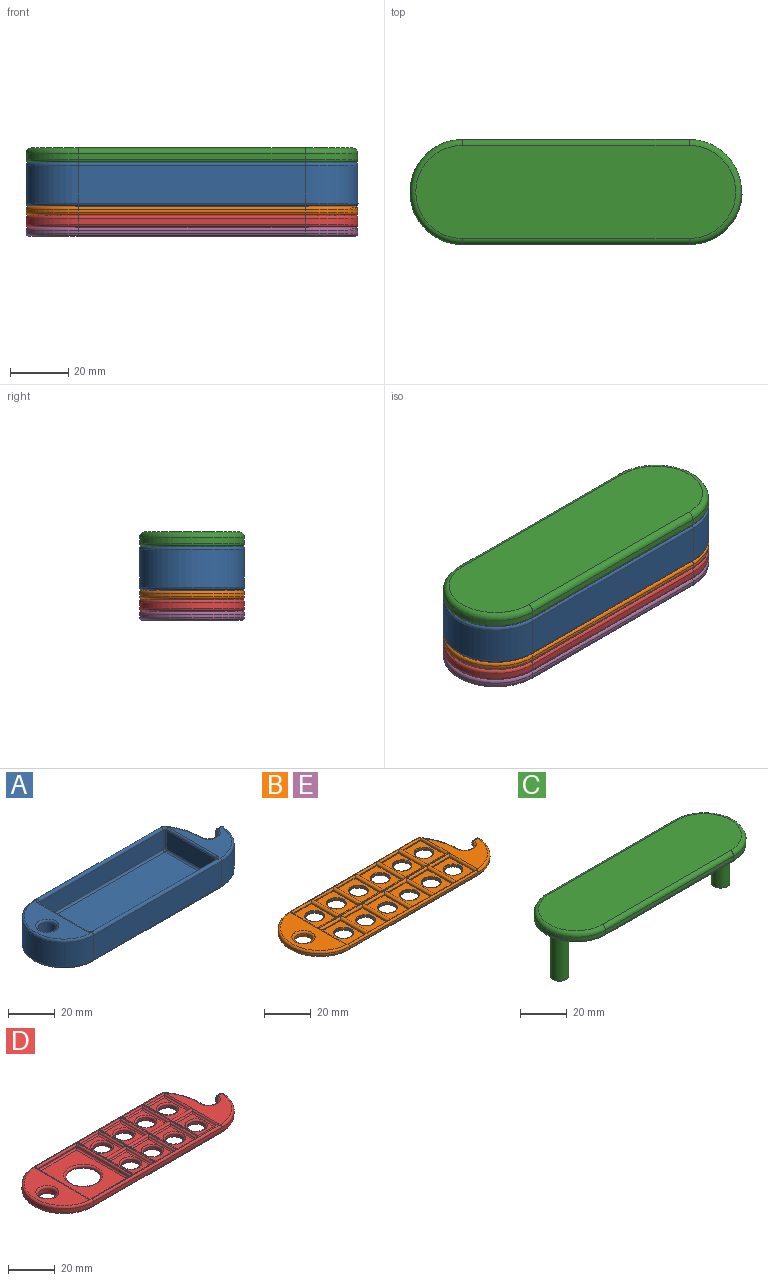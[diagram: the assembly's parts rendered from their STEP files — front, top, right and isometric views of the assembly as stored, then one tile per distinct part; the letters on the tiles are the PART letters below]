
ASSEMBLY  parts=5 mates=4
PART A: 58 faces, bbox 117x39x15 mm
  f0: plane 32.74x18.47mm, normal (0,0,1), area 225.4mm2, adj f28,f33,f34,f36,f37,f38,f50,f54
  f1: plane 1.39x0.57mm, normal (0,0,1), area 0.1mm2, adj f32,f33,f36
  f2: plane 77.49x13mm, normal (0,1,0), area 1007.4mm2, adj f3,f32,f44,f47
  f3: cylinder r=18mm len=36mm, axis (0,0,-1), area 735.1mm2, adj f2,f4,f42,f49
  f4: plane 78x13mm, normal (0,-1,0), area 1014mm2, adj f3,f5,f34,f40
  f5: cylinder r=18mm len=17.97mm, axis (0,0,-1), area 353.8mm2, adj f4,f39,f50,f55
  f6: plane 13x2.07mm, normal (0,1,0), area 26.9mm2, adj f41,f52,f54,f55
  f7: cylinder r=4mm len=13mm, axis (0,0,-1), area 152.9mm2, adj f8,f28,f43,f52
  f8: cylinder r=30mm len=17.59mm, axis (0,0,-1), area 244.3mm2, adj f7,f33,f45,f47
  f9: cylinder r=4mm len=13mm, axis (0,0,-1), area 326.7mm2, adj f51,f57
  f10: plane 111.97x34mm, normal (0,0,-1), area 3268.2mm2, adj f39,f40,f41,f42,f43,f44,f45,f51
  f11: plane 30x10mm, normal (1,0,0), area 300mm2, adj f17,f21,f22,f23
  f12: plane 75.5x10mm, normal (0,-1,0), area 755mm2, adj f20,f21,f31,f32
  f13: plane 30x10mm, normal (-1,0,0), area 300mm2, adj f25,f31,f35,f38
  f14: plane 75.5x10mm, normal (0,1,0), area 755mm2, adj f23,f24,f34,f35
  f15: plane 34x18mm, normal (0,0,1), area 343.1mm2, adj f22,f27,f29,f32,f34,f49,f57
  f16: plane 75.5x30mm, normal (0,0,1), area 2265mm2, adj f17,f20,f24,f25
  f17: cylinder r=1mm len=30mm, axis (0,-1,0), area 47.1mm2, adj f11,f16,f18,f19
  f18: sphere r=1mm, area 1.6mm2, adj f17,f20,f21
  f19: sphere r=1mm, area 1.6mm2, adj f17,f23,f24
  f20: cylinder r=1mm len=75.5mm, axis (-1,0,0), area 118.6mm2, adj f12,f16,f18,f26
  f21: cylinder r=1mm len=10mm, axis (0,0,-1), area 15.7mm2, adj f11,f12,f18,f27
  f22: cylinder r=1mm len=30mm, axis (0,-1,0), area 47.1mm2, adj f11,f15,f27,f29
  f23: cylinder r=1mm len=10mm, axis (0,0,1), area 15.7mm2, adj f11,f14,f19,f29
  f24: cylinder r=1mm len=75.5mm, axis (1,0,0), area 118.6mm2, adj f14,f16,f19,f30
  f25: cylinder r=1mm len=30mm, axis (0,1,0), area 47.1mm2, adj f13,f16,f26,f30
  f26: sphere r=1mm, area 1.6mm2, adj f20,f25,f31
  f27: torus R=2mm, axis (0,0,1), area 3.4mm2, adj f15,f21,f22,f32
  f28: torus R=5mm, axis (0,0,1), area 20.2mm2, adj f0,f7,f33,f53
  f29: torus R=2mm, axis (0,0,1), area 3.4mm2, adj f15,f22,f23,f34
  f30: sphere r=1mm, area 1.6mm2, adj f24,f25,f35
  f31: cylinder r=1mm len=10mm, axis (0,0,1), area 15.7mm2, adj f12,f13,f26,f36
  f32: cylinder r=1mm len=77.49mm, axis (-1,0,0), area 240.3mm2, adj f1,f2,f12,f15,f27,f36,f48,f49
  f33: torus R=29mm, axis (0,0,1), area 29.1mm2, adj f0,f1,f8,f28,f36,f48
  f34: cylinder r=1mm len=78mm, axis (1,0,0), area 241.1mm2, adj f0,f4,f14,f15,f29,f37,f49,f50
  f35: cylinder r=1mm len=10mm, axis (0,0,-1), area 15.7mm2, adj f13,f14,f30,f37
  f36: torus R=2mm, axis (0,0,1), area 3.4mm2, adj f0,f1,f31,f32,f33,f38
  f37: torus R=2mm, axis (0,0,1), area 3.4mm2, adj f0,f34,f35,f38
  f38: cylinder r=1mm len=30mm, axis (0,1,0), area 47.1mm2, adj f0,f13,f36,f37
  f39: torus R=17mm, axis (0,0,1), area 42.5mm2, adj f5,f10,f40,f41,f55
  f40: cylinder r=1mm len=78mm, axis (1,0,0), area 122.5mm2, adj f4,f10,f39,f42
  f41: cylinder r=1mm len=3.45mm, axis (-1,0,0), area 4.4mm2, adj f6,f10,f39,f43,f52,f55
  f42: torus R=17mm, axis (0,0,1), area 87mm2, adj f3,f10,f40,f44
  f43: torus R=5mm, axis (0,0,1), area 20.6mm2, adj f7,f10,f41,f45,f52
  f44: cylinder r=1mm len=77.49mm, axis (-1,0,0), area 121.7mm2, adj f2,f10,f42,f46
  f45: torus R=29mm, axis (0,0,1), area 29.2mm2, adj f8,f10,f43,f46
  f46: sphere r=1mm, area 0.9mm2, adj f44,f45,f47
  f47: cylinder r=1mm len=13mm, axis (0,0,-1), area 12.3mm2, adj f2,f8,f46,f48
  f48: sphere r=1mm, area 0.9mm2, adj f32,f33,f47
  f49: torus R=17mm, axis (0,0,1), area 87mm2, adj f3,f15,f32,f34
  f50: torus R=17mm, axis (0,0,1), area 41.9mm2, adj f0,f5,f34,f56
  f51: torus R=5mm, axis (0,0,1), area 43.1mm2, adj f9,f10
  f52: cylinder r=1mm len=13.66mm, axis (0,0,-1), area 18.3mm2, adj f6,f7,f41,f43,f53
  f53: sphere r=1mm, area 1.4mm2, adj f28,f52,f54
  f54: cylinder r=1mm len=2.07mm, axis (1,0,0), area 3.3mm2, adj f0,f6,f53,f56
  f55: cylinder r=1mm len=13.72mm, axis (0,0,-1), area 21.8mm2, adj f5,f6,f39,f41,f56
  f56: sphere r=1mm, area 1.6mm2, adj f50,f54,f55
  f57: torus R=5mm, axis (0,0,1), area 43.1mm2, adj f9,f15
PART B: 166 faces, bbox 116.9x39x3 mm
  f0: plane 78x1mm, normal (0,1,0), area 78mm2, adj f1,f6,f63,f74
  f1: cylinder r=18mm len=36mm, axis (0,0,-1), area 56.5mm2, adj f0,f2,f75,f90
  f2: plane 78x1mm, normal (0,-1,0), area 78mm2, adj f1,f3,f91,f96
  f3: cylinder r=18mm len=17.97mm, axis (0,0,-1), area 27.2mm2, adj f2,f97,f100,f103
  f4: plane 2.07x1mm, normal (0,1,0), area 2.1mm2, adj f88,f98,f99,f103
  f5: cylinder r=4mm len=7.92mm, axis (0,0,-1), area 11.8mm2, adj f6,f87,f88,f89
  f6: cylinder r=30mm len=18mm, axis (0,0,-1), area 19.3mm2, adj f0,f5,f72,f73
  f7: cylinder r=4mm len=8mm, axis (0,0,-1), area 25.1mm2, adj f104,f105
  f8: plane 111.97x33.95mm, normal (0,0,1), area 588.2mm2, adj f46,f47,f48,f49,f50,f60,f61,f65
  f9: plane 111.97x34mm, normal (0,0,-1), area 2325.7mm2, adj f34,f35,f36,f37,f38,f39,f40,f41
  f10: cylinder r=4mm len=8mm, axis (0,0,-1), area 16.3mm2, adj f44,f160
  f11: plane 14.82x10.82mm, normal (0,0,1), area 103.6mm2, adj f156,f157,f158,f159,f160
  f12: cylinder r=4mm len=8mm, axis (0,0,-1), area 16.3mm2, adj f45,f165
  f13: plane 14.82x10.82mm, normal (0,0,1), area 103.6mm2, adj f161,f162,f163,f164,f165
  f14: cylinder r=4mm len=8mm, axis (0,0,-1), area 16.3mm2, adj f43,f155
  f15: plane 14.82x10.82mm, normal (0,0,1), area 103.6mm2, adj f151,f152,f153,f154,f155
  f16: cylinder r=4mm len=8mm, axis (0,0,-1), area 16.3mm2, adj f40,f140
  f17: plane 14.82x10.82mm, normal (0,0,1), area 103.6mm2, adj f136,f137,f138,f139,f140
  f18: cylinder r=4mm len=8mm, axis (0,0,-1), area 16.3mm2, adj f39,f135
  f19: plane 14.82x10.82mm, normal (0,0,1), area 103.6mm2, adj f131,f132,f133,f134,f135
  f20: cylinder r=4mm len=8mm, axis (0,0,-1), area 16.3mm2, adj f38,f130
  f21: plane 14.82x10.82mm, normal (0,0,1), area 103.6mm2, adj f126,f127,f128,f129,f130
  f22: cylinder r=4mm len=8mm, axis (0,0,-1), area 16.3mm2, adj f34,f110
  f23: plane 14.82x10.82mm, normal (0,0,1), area 103.6mm2, adj f106,f107,f108,f109,f110
  f24: cylinder r=4mm len=8mm, axis (0,0,-1), area 16.3mm2, adj f42,f150
  f25: plane 14.82x10.82mm, normal (0,0,1), area 103.6mm2, adj f146,f147,f148,f149,f150
  f26: cylinder r=4mm len=8mm, axis (0,0,-1), area 16.3mm2, adj f41,f145
  f27: plane 14.82x10.82mm, normal (0,0,1), area 103.6mm2, adj f141,f142,f143,f144,f145
  f28: cylinder r=4mm len=8mm, axis (0,0,-1), area 16.3mm2, adj f37,f125
  f29: plane 14.82x10.82mm, normal (0,0,1), area 103.6mm2, adj f121,f122,f123,f124,f125
  f30: cylinder r=4mm len=8mm, axis (0,0,-1), area 16.3mm2, adj f36,f120
  f31: plane 14.82x10.82mm, normal (0,0,1), area 103.6mm2, adj f116,f117,f118,f119,f120
  f32: cylinder r=4mm len=8mm, axis (0,0,-1), area 16.3mm2, adj f35,f115
  f33: plane 14.82x10.82mm, normal (0,0,1), area 103.6mm2, adj f111,f112,f113,f114,f115
  f34: torus R=5mm, axis (0,0,1), area 43.1mm2, adj f9,f22
  f35: torus R=5mm, axis (0,0,1), area 43.1mm2, adj f9,f32
  f36: torus R=5mm, axis (0,0,1), area 43.1mm2, adj f9,f30
  f37: torus R=5mm, axis (0,0,1), area 43.1mm2, adj f9,f28
  f38: torus R=5mm, axis (0,0,1), area 43.1mm2, adj f9,f20
  f39: torus R=5mm, axis (0,0,1), area 43.1mm2, adj f9,f18
  f40: torus R=5mm, axis (0,0,1), area 43.1mm2, adj f9,f16
  f41: torus R=5mm, axis (0,0,1), area 43.1mm2, adj f9,f26
  f42: torus R=5mm, axis (0,0,1), area 43.1mm2, adj f9,f24
  f43: torus R=5mm, axis (0,0,1), area 43.1mm2, adj f9,f14
  f44: torus R=5mm, axis (0,0,1), area 43.1mm2, adj f9,f10
  f45: torus R=5mm, axis (0,0,1), area 43.1mm2, adj f9,f12
  f46: cylinder r=1mm len=13.3mm, axis (1,0,0), area 17.5mm2, adj f8,f51,f53,f127
  f47: cylinder r=1mm len=13.3mm, axis (1,0,0), area 17.5mm2, adj f8,f53,f55,f132
  f48: cylinder r=1mm len=13.3mm, axis (1,0,0), area 17.5mm2, adj f8,f55,f57,f137
  f49: cylinder r=1mm len=13.3mm, axis (1,0,0), area 17.5mm2, adj f8,f57,f59,f152
  f50: cylinder r=1mm len=13.3mm, axis (1,0,0), area 17.5mm2, adj f8,f51,f61,f107
  f51: cylinder r=1mm len=17.05mm, axis (0,-1,0), area 46.5mm2, adj f46,f50,f52,f62,f63,f109,f126
  f52: cylinder r=1mm len=12.8mm, axis (-1,0,0), area 14.2mm2, adj f51,f53,f63,f128
  f53: cylinder r=1mm len=17.05mm, axis (0,-1,0), area 46.5mm2, adj f46,f47,f52,f54,f63,f129,f131
  f54: cylinder r=1mm len=12.8mm, axis (-1,0,0), area 14.2mm2, adj f53,f55,f63,f133
  f55: cylinder r=1mm len=17.05mm, axis (0,-1,0), area 46.5mm2, adj f47,f48,f54,f56,f63,f134,f136
  f56: cylinder r=1mm len=12.8mm, axis (-1,0,0), area 14.2mm2, adj f55,f57,f63,f138
  f57: cylinder r=1mm len=17.05mm, axis (0,-1,0), area 46.5mm2, adj f48,f49,f56,f58,f63,f139,f151
  f58: cylinder r=1mm len=12.8mm, axis (-1,0,0), area 14.2mm2, adj f57,f59,f63,f153
  f59: cylinder r=1mm len=17.05mm, axis (0,-1,0), area 46.5mm2, adj f49,f58,f60,f63,f64,f154,f158
  f60: cylinder r=1mm len=13.3mm, axis (1,0,0), area 17.5mm2, adj f8,f59,f65,f156
  f61: cylinder r=1mm len=16.73mm, axis (0,1,0), area 22.6mm2, adj f8,f50,f62,f72,f106
  f62: cylinder r=1mm len=12.48mm, axis (-1,0,0), area 14.1mm2, adj f51,f61,f63,f72,f108
  f63: cylinder r=1mm len=78mm, axis (1,0,0), area 103mm2, adj f0,f51,f52,f53,f54,f55,f56,f57
  f64: cylinder r=1mm len=12.79mm, axis (-1,0,0), area 14.2mm2, adj f59,f63,f65,f75,f159
  f65: cylinder r=1mm len=17.04mm, axis (0,-1,0), area 23.3mm2, adj f8,f60,f64,f75,f157
  f66: cylinder r=1mm len=17.04mm, axis (0,-1,0), area 23.3mm2, adj f8,f67,f75,f76,f164
  f67: cylinder r=1mm len=13.3mm, axis (-1,0,0), area 17.5mm2, adj f8,f66,f77,f162
  f68: cylinder r=1mm len=13.3mm, axis (-1,0,0), area 17.5mm2, adj f8,f77,f79,f147
  f69: cylinder r=1mm len=13.3mm, axis (-1,0,0), area 17.5mm2, adj f8,f79,f81,f142
  f70: cylinder r=1mm len=13.3mm, axis (-1,0,0), area 17.5mm2, adj f8,f81,f83,f122
  f71: cylinder r=1mm len=13.3mm, axis (-1,0,0), area 17.5mm2, adj f8,f83,f85,f117
  f72: torus R=29mm, axis (0,0,1), area 28.9mm2, adj f6,f8,f61,f62,f63,f87
  f73: torus R=29mm, axis (0,0,1), area 29.7mm2, adj f6,f9,f74,f89
  f74: cylinder r=1mm len=78mm, axis (-1,0,0), area 122.2mm2, adj f0,f9,f73,f90
  f75: torus R=17mm, axis (0,0,1), area 86.6mm2, adj f1,f8,f63,f64,f65,f66,f76,f91
  f76: cylinder r=1mm len=12.79mm, axis (1,0,0), area 14.2mm2, adj f66,f75,f77,f91,f163
  f77: cylinder r=1mm len=17.05mm, axis (0,1,0), area 46.5mm2, adj f67,f68,f76,f78,f91,f149,f161
  f78: cylinder r=1mm len=12.8mm, axis (1,0,0), area 14.2mm2, adj f77,f79,f91,f148
  f79: cylinder r=1mm len=17.05mm, axis (0,1,0), area 46.5mm2, adj f68,f69,f78,f80,f91,f144,f146
  f80: cylinder r=1mm len=12.8mm, axis (1,0,0), area 14.2mm2, adj f79,f81,f91,f143
  f81: cylinder r=1mm len=17.05mm, axis (0,1,0), area 46.5mm2, adj f69,f70,f80,f82,f91,f124,f141
  f82: cylinder r=1mm len=12.8mm, axis (1,0,0), area 14.2mm2, adj f81,f83,f91,f123
  f83: cylinder r=1mm len=17.05mm, axis (0,1,0), area 46.5mm2, adj f70,f71,f82,f84,f91,f119,f121
  f84: cylinder r=1mm len=12.8mm, axis (1,0,0), area 14.2mm2, adj f83,f85,f91,f118
  f85: cylinder r=1mm len=17.05mm, axis (0,1,0), area 46.5mm2, adj f71,f84,f86,f91,f92,f114,f116
  f86: cylinder r=1mm len=13.3mm, axis (-1,0,0), area 17.5mm2, adj f8,f85,f93,f112
  f87: torus R=5mm, axis (0,0,1), area 20.2mm2, adj f5,f8,f72,f94
  f88: cylinder r=1mm len=1mm, axis (0,0,-1), area 1.4mm2, adj f4,f5,f94,f95
  f89: torus R=5mm, axis (0,0,1), area 20.2mm2, adj f5,f9,f73,f95
  f90: torus R=17mm, axis (0,0,1), area 87mm2, adj f1,f9,f74,f96
  f91: cylinder r=1mm len=78mm, axis (-1,0,0), area 103.1mm2, adj f2,f75,f76,f77,f78,f79,f80,f81
  f92: cylinder r=1mm len=12.8mm, axis (1,0,0), area 14.2mm2, adj f85,f91,f93,f97,f113
  f93: cylinder r=1mm len=17.05mm, axis (0,1,0), area 23.3mm2, adj f8,f86,f92,f97,f111
  f94: sphere r=1mm, area 1.4mm2, adj f87,f88,f98
  f95: sphere r=1mm, area 1.4mm2, adj f88,f89,f99
  f96: cylinder r=1mm len=78mm, axis (1,0,0), area 122.5mm2, adj f2,f9,f90,f100
  f97: torus R=17mm, axis (0,0,1), area 41.7mm2, adj f3,f8,f91,f92,f93,f101
  f98: cylinder r=1mm len=2.07mm, axis (1,0,0), area 3.3mm2, adj f4,f8,f94,f101
  f99: cylinder r=1mm len=2.07mm, axis (-1,0,0), area 3.3mm2, adj f4,f9,f95,f102
  f100: torus R=17mm, axis (0,0,1), area 41.9mm2, adj f3,f9,f96,f102
  f101: sphere r=1mm, area 1.6mm2, adj f97,f98,f103
  f102: sphere r=1mm, area 1.6mm2, adj f99,f100,f103
  f103: cylinder r=1mm len=1.06mm, axis (0,0,-1), area 1.6mm2, adj f3,f4,f101,f102
  f104: torus R=5mm, axis (0,0,1), area 43.1mm2, adj f7,f9
  f105: torus R=5mm, axis (0,0,1), area 43.1mm2, adj f7,f8
  f106: cylinder r=0.25mm len=15.31mm, axis (0,1,0), area 5.5mm2, adj f23,f61,f107,f108
  f107: cylinder r=0.25mm len=11.31mm, axis (1,0,0), area 4mm2, adj f23,f50,f106,f109
  f108: cylinder r=0.25mm len=11.31mm, axis (-1,0,0), area 4mm2, adj f23,f62,f106,f109
  f109: cylinder r=0.25mm len=15.31mm, axis (0,-1,0), area 5.5mm2, adj f23,f51,f107,f108
  f110: torus R=4.25mm, axis (0,0,1), area 10.1mm2, adj f22,f23
  f111: cylinder r=0.25mm len=15.31mm, axis (0,1,0), area 5.5mm2, adj f33,f93,f112,f113
  f112: cylinder r=0.25mm len=11.31mm, axis (-1,0,0), area 4mm2, adj f33,f86,f111,f114
  f113: cylinder r=0.25mm len=11.31mm, axis (1,0,0), area 4mm2, adj f33,f92,f111,f114
  f114: cylinder r=0.25mm len=15.31mm, axis (0,1,0), area 5.5mm2, adj f33,f85,f112,f113
  f115: torus R=4.25mm, axis (0,0,1), area 10.1mm2, adj f32,f33
  f116: cylinder r=0.25mm len=15.31mm, axis (0,1,0), area 5.5mm2, adj f31,f85,f117,f118
  f117: cylinder r=0.25mm len=11.31mm, axis (-1,0,0), area 4mm2, adj f31,f71,f116,f119
  f118: cylinder r=0.25mm len=11.31mm, axis (1,0,0), area 4mm2, adj f31,f84,f116,f119
  f119: cylinder r=0.25mm len=15.31mm, axis (0,1,0), area 5.5mm2, adj f31,f83,f117,f118
  f120: torus R=4.25mm, axis (0,0,1), area 10.1mm2, adj f30,f31
  f121: cylinder r=0.25mm len=15.31mm, axis (0,1,0), area 5.5mm2, adj f29,f83,f122,f123
  f122: cylinder r=0.25mm len=11.31mm, axis (-1,0,0), area 4mm2, adj f29,f70,f121,f124
  f123: cylinder r=0.25mm len=11.31mm, axis (1,0,0), area 4mm2, adj f29,f82,f121,f124
  f124: cylinder r=0.25mm len=15.31mm, axis (0,1,0), area 5.5mm2, adj f29,f81,f122,f123
  f125: torus R=4.25mm, axis (0,0,1), area 10.1mm2, adj f28,f29
  f126: cylinder r=0.25mm len=15.31mm, axis (0,-1,0), area 5.5mm2, adj f21,f51,f127,f128
  f127: cylinder r=0.25mm len=11.31mm, axis (1,0,0), area 4mm2, adj f21,f46,f126,f129
  f128: cylinder r=0.25mm len=11.31mm, axis (-1,0,0), area 4mm2, adj f21,f52,f126,f129
  f129: cylinder r=0.25mm len=15.31mm, axis (0,-1,0), area 5.5mm2, adj f21,f53,f127,f128
  f130: torus R=4.25mm, axis (0,0,1), area 10.1mm2, adj f20,f21
  f131: cylinder r=0.25mm len=15.31mm, axis (0,-1,0), area 5.5mm2, adj f19,f53,f132,f133
  f132: cylinder r=0.25mm len=11.31mm, axis (1,0,0), area 4mm2, adj f19,f47,f131,f134
  f133: cylinder r=0.25mm len=11.31mm, axis (-1,0,0), area 4mm2, adj f19,f54,f131,f134
  f134: cylinder r=0.25mm len=15.31mm, axis (0,-1,0), area 5.5mm2, adj f19,f55,f132,f133
  f135: torus R=4.25mm, axis (0,0,1), area 10.1mm2, adj f18,f19
  f136: cylinder r=0.25mm len=15.31mm, axis (0,-1,0), area 5.5mm2, adj f17,f55,f137,f138
  f137: cylinder r=0.25mm len=11.31mm, axis (1,0,0), area 4mm2, adj f17,f48,f136,f139
  f138: cylinder r=0.25mm len=11.31mm, axis (-1,0,0), area 4mm2, adj f17,f56,f136,f139
  f139: cylinder r=0.25mm len=15.31mm, axis (0,-1,0), area 5.5mm2, adj f17,f57,f137,f138
  f140: torus R=4.25mm, axis (0,0,1), area 10.1mm2, adj f16,f17
  f141: cylinder r=0.25mm len=15.31mm, axis (0,1,0), area 5.5mm2, adj f27,f81,f142,f143
  f142: cylinder r=0.25mm len=11.31mm, axis (-1,0,0), area 4mm2, adj f27,f69,f141,f144
  f143: cylinder r=0.25mm len=11.31mm, axis (1,0,0), area 4mm2, adj f27,f80,f141,f144
  f144: cylinder r=0.25mm len=15.31mm, axis (0,1,0), area 5.5mm2, adj f27,f79,f142,f143
  f145: torus R=4.25mm, axis (0,0,1), area 10.1mm2, adj f26,f27
  f146: cylinder r=0.25mm len=15.31mm, axis (0,1,0), area 5.5mm2, adj f25,f79,f147,f148
  f147: cylinder r=0.25mm len=11.31mm, axis (-1,0,0), area 4mm2, adj f25,f68,f146,f149
  f148: cylinder r=0.25mm len=11.31mm, axis (1,0,0), area 4mm2, adj f25,f78,f146,f149
  f149: cylinder r=0.25mm len=15.31mm, axis (0,1,0), area 5.5mm2, adj f25,f77,f147,f148
  f150: torus R=4.25mm, axis (0,0,1), area 10.1mm2, adj f24,f25
  f151: cylinder r=0.25mm len=15.31mm, axis (0,-1,0), area 5.5mm2, adj f15,f57,f152,f153
  f152: cylinder r=0.25mm len=11.31mm, axis (1,0,0), area 4mm2, adj f15,f49,f151,f154
  f153: cylinder r=0.25mm len=11.31mm, axis (-1,0,0), area 4mm2, adj f15,f58,f151,f154
  f154: cylinder r=0.25mm len=15.31mm, axis (0,-1,0), area 5.5mm2, adj f15,f59,f152,f153
  f155: torus R=4.25mm, axis (0,0,1), area 10.1mm2, adj f14,f15
  f156: cylinder r=0.25mm len=11.31mm, axis (1,0,0), area 4mm2, adj f11,f60,f157,f158
  f157: cylinder r=0.25mm len=15.31mm, axis (0,-1,0), area 5.5mm2, adj f11,f65,f156,f159
  f158: cylinder r=0.25mm len=15.31mm, axis (0,-1,0), area 5.5mm2, adj f11,f59,f156,f159
  f159: cylinder r=0.25mm len=11.31mm, axis (-1,0,0), area 4mm2, adj f11,f64,f157,f158
  f160: torus R=4.25mm, axis (0,0,1), area 10.1mm2, adj f10,f11
  f161: cylinder r=0.25mm len=15.31mm, axis (0,1,0), area 5.5mm2, adj f13,f77,f162,f163
  f162: cylinder r=0.25mm len=11.31mm, axis (-1,0,0), area 4mm2, adj f13,f67,f161,f164
  f163: cylinder r=0.25mm len=11.31mm, axis (1,0,0), area 4mm2, adj f13,f76,f161,f164
  f164: cylinder r=0.25mm len=15.31mm, axis (0,-1,0), area 5.5mm2, adj f13,f66,f162,f163
  f165: torus R=4.25mm, axis (0,0,1), area 10.1mm2, adj f12,f13
PART C: 26 faces, bbox 116.8x39x30 mm
  f0: cylinder r=18mm len=36mm, axis (0,0,-1), area 113.1mm2, adj f1,f3,f18,f24
  f1: plane 77.81x2mm, normal (0,1,0), area 155.6mm2, adj f0,f2,f19,f22
  f2: cylinder r=18mm len=36mm, axis (0,0,-1), area 113.1mm2, adj f1,f3,f21,f23
  f3: plane 77.81x2mm, normal (0,-1,0), area 155.6mm2, adj f0,f2,f20,f25
  f4: plane 109.81x32mm, normal (0,0,1), area 3294.2mm2, adj f22,f23,f24,f25
  f5: plane 111.81x34mm, normal (0,0,-1), area 3396.4mm2, adj f14,f16,f18,f19,f20,f21
  f6: cylinder r=2mm len=24mm, axis (0,0,1), area 301.6mm2, adj f8,f17
  f7: cylinder r=4mm len=24mm, axis (0,0,1), area 603.2mm2, adj f8,f16
  f8: plane 8x8mm, normal (0,0,-1), area 37.7mm2, adj f6,f7
  f9: plane 2x2mm, normal (0,0,-1), area 3.1mm2, adj f17
  f10: cylinder r=2mm len=24mm, axis (0,0,1), area 301.6mm2, adj f12,f15
  f11: cylinder r=4mm len=24mm, axis (0,0,1), area 603.2mm2, adj f12,f14
  f12: plane 8x8mm, normal (0,0,-1), area 37.7mm2, adj f10,f11
  f13: plane 2x2mm, normal (0,0,-1), area 3.1mm2, adj f15
  f14: torus R=5mm, axis (0,0,1), area 43.1mm2, adj f5,f11
  f15: torus R=1mm, axis (0,0,1), area 16.2mm2, adj f10,f13
  f16: torus R=5mm, axis (0,0,1), area 43.1mm2, adj f5,f7
  f17: torus R=1mm, axis (0,0,1), area 16.2mm2, adj f6,f9
  f18: torus R=17mm, axis (0,0,1), area 87mm2, adj f0,f5,f19,f20
  f19: cylinder r=1mm len=77.81mm, axis (-1,0,0), area 122.2mm2, adj f1,f5,f18,f21
  f20: cylinder r=1mm len=77.81mm, axis (1,0,0), area 122.2mm2, adj f3,f5,f18,f21
  f21: torus R=17mm, axis (0,0,1), area 87mm2, adj f2,f5,f19,f20
  f22: cylinder r=2mm len=77.81mm, axis (1,0,0), area 244.4mm2, adj f1,f4,f23,f24
  f23: torus R=16mm, axis (0,0,1), area 170.5mm2, adj f2,f4,f22,f25
  f24: torus R=16mm, axis (0,0,1), area 170.5mm2, adj f0,f4,f22,f25
  f25: cylinder r=2mm len=77.81mm, axis (-1,0,0), area 244.4mm2, adj f3,f4,f23,f24
PART D: 144 faces, bbox 116.9x39x4.3 mm
  f0: plane 34x0.3mm, normal (0,0,1), area 10.2mm2, adj f51,f55,f85,f88,f93,f97
  f1: plane 34x0.3mm, normal (0,0,1), area 10.2mm2, adj f51,f55,f78,f81,f92,f94
  f2: plane 34x30.12mm, normal (0,0,1), area 262mm2, adj f13,f48,f49,f51,f52,f54,f55,f72
  f3: plane 32.3x0.4mm, normal (1,0,0), area 12.9mm2, adj f4,f14,f69,f98
  f4: plane 24.3x0.4mm, normal (0,-1,0), area 9.7mm2, adj f3,f5,f68,f99,f100
  f5: plane 32.3x0.4mm, normal (-1,0,0), area 12.9mm2, adj f4,f14,f70,f101
  f6: cylinder r=4mm len=7.92mm, axis (0,0,-1), area 24mm2, adj f7,f42,f47,f52
  f7: cylinder r=25mm len=17.77mm, axis (0,0,-1), area 38.4mm2, adj f6,f8,f40,f54
  f8: plane 78x2mm, normal (0,1,0), area 156mm2, adj f7,f9,f38,f55
  f9: cylinder r=18mm len=36mm, axis (0,0,-1), area 113.1mm2, adj f8,f10,f36,f53
  f10: plane 78x2mm, normal (0,-1,0), area 156mm2, adj f9,f11,f37,f51
  f11: cylinder r=18mm len=17.97mm, axis (0,0,-1), area 54.4mm2, adj f10,f39,f44,f49
  f12: cylinder r=4mm len=8mm, axis (0,0,-1), area 50.3mm2, adj f65,f66
  f13: plane 13x0.4mm, normal (0,1,0), area 4.8mm2, adj f2,f72,f73,f120
  f14: plane 24.3x0.45mm, normal (0,1,0), area 10.9mm2, adj f3,f5,f71,f98,f101,f143
  f15: plane 2.07x2mm, normal (0,1,0), area 4.1mm2, adj f43,f44,f47,f48
  f16: plane 42.25x34mm, normal (0,0,1), area 351.2mm2, adj f51,f53,f55,f66,f86,f90,f98,f101
  f17: plane 111.97x34mm, normal (0,0,-1), area 2416.9mm2, adj f36,f37,f38,f39,f40,f42,f43,f56
  f18: cylinder r=7.5mm len=15mm, axis (0,0,-1), area 2.4mm2, adj f64,f67
  f19: plane 30.6x22.6mm, normal (0,0,1), area 472.5mm2, adj f67,f68,f69,f70,f71
  f20: cylinder r=4mm len=8mm, axis (0,0,-1), area 25.1mm2, adj f61,f132
  f21: plane 13.83x9.83mm, normal (0,0,1), area 63.5mm2, adj f128,f129,f130,f131,f132
  f22: cylinder r=4mm len=8mm, axis (0,0,-1), area 25.1mm2, adj f58,f117
  f23: plane 13.83x9.83mm, normal (0,0,1), area 63.5mm2, adj f113,f114,f115,f116,f117
  f24: cylinder r=4mm len=8mm, axis (0,0,-1), area 25.1mm2, adj f60,f127
  f25: plane 13.83x9.81mm, normal (0,0,1), area 63.3mm2, adj f123,f124,f125,f126,f127
  f26: cylinder r=4mm len=8mm, axis (0,0,-1), area 25.1mm2, adj f59,f122
  f27: plane 13.76x9.83mm, normal (0,0,1), area 62.8mm2, adj f118,f119,f120,f121,f122
  f28: cylinder r=4mm len=8mm, axis (0,0,-1), area 25.1mm2, adj f56,f107
  f29: plane 13.83x9.83mm, normal (0,0,1), area 63.5mm2, adj f103,f104,f105,f106,f107
  f30: cylinder r=4mm len=8mm, axis (0,0,-1), area 25.1mm2, adj f62,f133
  f31: plane 13.83x9.83mm, normal (0,0,1), area 63.5mm2, adj f133,f134,f135,f136,f137
  f32: cylinder r=4mm len=8mm, axis (0,0,-1), area 25.1mm2, adj f57,f112
  f33: plane 13.83x9.83mm, normal (0,0,1), area 63.5mm2, adj f108,f109,f110,f111,f112
  f34: cylinder r=4mm len=8mm, axis (0,0,-1), area 25.1mm2, adj f63,f142
  f35: plane 13.83x9.83mm, normal (0,0,1), area 63.5mm2, adj f138,f139,f140,f141,f142
  f36: torus R=17mm, axis (0,0,1), area 87mm2, adj f9,f17,f37,f38
  f37: cylinder r=1mm len=78mm, axis (1,0,0), area 122.5mm2, adj f10,f17,f36,f39
  f38: cylinder r=1mm len=78mm, axis (-1,0,0), area 122.2mm2, adj f8,f17,f36,f40
  f39: torus R=17mm, axis (0,0,1), area 41.9mm2, adj f11,f17,f37,f41
  f40: torus R=24mm, axis (0,0,1), area 29.4mm2, adj f7,f17,f38,f42
  f41: sphere r=1mm, area 2.2mm2, adj f39,f43,f44
  f42: torus R=5mm, axis (0,0,1), area 20.6mm2, adj f6,f17,f40,f45
  f43: cylinder r=1mm len=2.07mm, axis (-1,0,0), area 3.3mm2, adj f15,f17,f41,f45
  f44: cylinder r=1mm len=2mm, axis (0,0,-1), area 3.3mm2, adj f11,f15,f41,f46
  f45: sphere r=1mm, area 1.4mm2, adj f42,f43,f47
  f46: sphere r=1mm, area 1.6mm2, adj f44,f48,f49
  f47: cylinder r=1mm len=2mm, axis (0,0,-1), area 2.7mm2, adj f6,f15,f45,f50
  f48: cylinder r=1mm len=2.07mm, axis (1,0,0), area 3.3mm2, adj f2,f15,f46,f50
  f49: torus R=17mm, axis (0,0,1), area 41.9mm2, adj f2,f11,f46,f51
  f50: sphere r=1mm, area 2.6mm2, adj f47,f48,f52
  f51: cylinder r=1mm len=78mm, axis (-1,0,0), area 122.5mm2, adj f0,f1,f2,f10,f16,f49,f53,f83
  f52: torus R=5mm, axis (0,0,1), area 20.6mm2, adj f2,f6,f50,f54
  f53: torus R=17mm, axis (0,0,1), area 86.9mm2, adj f9,f16,f51,f55,f98,f99
  f54: torus R=24mm, axis (0,0,1), area 29.3mm2, adj f2,f7,f52,f55,f74,f102
  f55: cylinder r=1mm len=78mm, axis (1,0,0), area 122.2mm2, adj f0,f1,f2,f8,f16,f53,f54,f74
  f56: torus R=5mm, axis (0,0,1), area 43.1mm2, adj f17,f28
  f57: torus R=5mm, axis (0,0,1), area 43.1mm2, adj f17,f32
  f58: torus R=5mm, axis (0,0,1), area 43.1mm2, adj f17,f22
  f59: torus R=5mm, axis (0,0,1), area 43.1mm2, adj f17,f26
  f60: torus R=5mm, axis (0,0,1), area 43.1mm2, adj f17,f24
  f61: torus R=5mm, axis (0,0,1), area 43.1mm2, adj f17,f20
  f62: torus R=5mm, axis (0,0,1), area 43.1mm2, adj f17,f30
  f63: torus R=5mm, axis (0,0,1), area 43.1mm2, adj f17,f34
  f64: torus R=8.5mm, axis (0,0,1), area 77.6mm2, adj f17,f18
  f65: torus R=5mm, axis (0,0,1), area 43.1mm2, adj f12,f17
  f66: torus R=5mm, axis (0,0,1), area 43.1mm2, adj f12,f16
  f67: torus R=8.35mm, axis (0,0,1), area 65.5mm2, adj f18,f19
  f68: cylinder r=0.85mm len=24.3mm, axis (1,0,0), area 31.3mm2, adj f4,f19,f69,f70
  f69: cylinder r=0.85mm len=32.3mm, axis (0,1,0), area 42mm2, adj f3,f19,f68,f71
  f70: cylinder r=0.85mm len=32.3mm, axis (0,-1,0), area 42mm2, adj f5,f19,f68,f71
  f71: cylinder r=0.85mm len=24.3mm, axis (-1,0,0), area 31.3mm2, adj f14,f19,f69,f70
  f72: cylinder r=0.85mm len=16.15mm, axis (0,1,0), area 17.3mm2, adj f2,f13,f75,f118,f120
  f73: cylinder r=0.85mm len=16.15mm, axis (0,-1,0), area 17.3mm2, adj f2,f13,f75,f120,f121
  f74: cylinder r=0.85mm len=12.78mm, axis (-1,0,0), area 13.2mm2, adj f54,f55,f76,f102,f125,f126
  f75: cylinder r=0.85mm len=13mm, axis (-1,0,0), area 26.5mm2, adj f2,f72,f73,f76,f102,f119,f123,f125
  f76: cylinder r=0.85mm len=17mm, axis (0,-1,0), area 17.8mm2, adj f2,f74,f75,f124
  f77: cylinder r=0.85mm len=13mm, axis (-1,0,0), area 13.4mm2, adj f55,f78,f79,f129
  f78: cylinder r=0.85mm len=17mm, axis (0,-1,0), area 17.8mm2, adj f1,f77,f80,f131
  f79: cylinder r=0.85mm len=17mm, axis (0,1,0), area 17.8mm2, adj f2,f77,f80,f128
  f80: cylinder r=0.85mm len=13mm, axis (1,0,0), area 26.8mm2, adj f78,f79,f81,f82,f114,f130
  f81: cylinder r=0.85mm len=17mm, axis (0,-1,0), area 17.8mm2, adj f1,f80,f83,f116
  f82: cylinder r=0.85mm len=17mm, axis (0,1,0), area 17.8mm2, adj f2,f80,f83,f113
  f83: cylinder r=0.85mm len=13mm, axis (1,0,0), area 13.4mm2, adj f51,f81,f82,f115
  f84: cylinder r=0.85mm len=13mm, axis (1,0,0), area 13.4mm2, adj f51,f85,f86,f105
  f85: cylinder r=0.85mm len=17mm, axis (0,1,0), area 17.8mm2, adj f0,f84,f89,f103
  f86: cylinder r=0.85mm len=17mm, axis (0,-1,0), area 17.8mm2, adj f16,f84,f89,f106
  f87: cylinder r=0.85mm len=13mm, axis (-1,0,0), area 13.4mm2, adj f55,f88,f90,f139
  f88: cylinder r=0.85mm len=17mm, axis (0,1,0), area 17.8mm2, adj f0,f87,f89,f138
  f89: cylinder r=0.85mm len=13mm, axis (-1,0,0), area 26.8mm2, adj f85,f86,f88,f90,f104,f140
  f90: cylinder r=0.85mm len=17mm, axis (0,-1,0), area 17.8mm2, adj f16,f87,f89,f141
  f91: cylinder r=0.85mm len=13mm, axis (1,0,0), area 13.4mm2, adj f51,f92,f93,f110
  f92: cylinder r=0.85mm len=17mm, axis (0,1,0), area 17.8mm2, adj f1,f91,f95,f108
  f93: cylinder r=0.85mm len=17mm, axis (0,-1,0), area 17.8mm2, adj f0,f91,f95,f111
  f94: cylinder r=0.85mm len=17mm, axis (0,1,0), area 17.8mm2, adj f1,f95,f96,f134
  f95: cylinder r=0.85mm len=13mm, axis (-1,0,0), area 26.8mm2, adj f92,f93,f94,f97,f109,f136
  f96: cylinder r=0.85mm len=13mm, axis (-1,0,0), area 13.4mm2, adj f55,f94,f97,f135
  f97: cylinder r=0.85mm len=17mm, axis (0,-1,0), area 17.8mm2, adj f0,f95,f96,f137
  f98: cylinder r=0.85mm len=34.08mm, axis (0,-1,0), area 43.9mm2, adj f3,f14,f16,f53,f99,f143
  f99: bspline ~1.9x1.18mm, area 0.7mm2, adj f4,f53,f98,f100
  f100: cylinder r=0.85mm len=24.95mm, axis (-1,0,0), area 32.7mm2, adj f4,f55,f99,f101
  f101: cylinder r=0.85mm len=33.95mm, axis (0,1,0), area 43.9mm2, adj f5,f14,f16,f100,f143
  f102: cylinder r=0.8mm len=16.82mm, axis (0,1,0), area 17mm2, adj f2,f54,f74,f75,f125
  f103: cylinder r=0.8mm len=15.36mm, axis (0,1,0), area 15.1mm2, adj f29,f85,f104,f105
  f104: cylinder r=0.8mm len=11.36mm, axis (-1,0,0), area 11mm2, adj f29,f89,f103,f106
  f105: cylinder r=0.8mm len=11.36mm, axis (1,0,0), area 11mm2, adj f29,f84,f103,f106
  f106: cylinder r=0.8mm len=15.36mm, axis (0,-1,0), area 15.1mm2, adj f29,f86,f104,f105
  f107: torus R=4.8mm, axis (0,0,1), area 33.9mm2, adj f28,f29
  f108: cylinder r=0.8mm len=15.36mm, axis (0,1,0), area 15.1mm2, adj f33,f92,f109,f110
  f109: cylinder r=0.8mm len=11.36mm, axis (-1,0,0), area 11mm2, adj f33,f95,f108,f111
  f110: cylinder r=0.8mm len=11.36mm, axis (1,0,0), area 11mm2, adj f33,f91,f108,f111
  f111: cylinder r=0.8mm len=15.36mm, axis (0,-1,0), area 15.1mm2, adj f33,f93,f109,f110
  f112: torus R=4.8mm, axis (0,0,1), area 33.9mm2, adj f32,f33
  f113: cylinder r=0.8mm len=15.36mm, axis (0,1,0), area 15.1mm2, adj f23,f82,f114,f115
  f114: cylinder r=0.8mm len=11.36mm, axis (1,0,0), area 11mm2, adj f23,f80,f113,f116
  f115: cylinder r=0.8mm len=11.36mm, axis (1,0,0), area 11mm2, adj f23,f83,f113,f116
  f116: cylinder r=0.8mm len=15.36mm, axis (0,-1,0), area 15.1mm2, adj f23,f81,f114,f115
  f117: torus R=4.8mm, axis (0,0,1), area 33.9mm2, adj f22,f23
  f118: cylinder r=0.8mm len=15.3mm, axis (0,1,0), area 15.1mm2, adj f27,f72,f119,f120
  f119: cylinder r=0.8mm len=11.36mm, axis (-1,0,0), area 11mm2, adj f27,f75,f118,f121
  f120: cylinder r=0.8mm len=11.56mm, axis (-1,0,0), area 13.5mm2, adj f13,f27,f72,f73,f118,f121
  f121: cylinder r=0.8mm len=15.3mm, axis (0,-1,0), area 15.1mm2, adj f27,f73,f119,f120
  f122: torus R=4.8mm, axis (0,0,1), area 33.9mm2, adj f26,f27
  f123: cylinder r=0.8mm len=11.35mm, axis (-1,0,0), area 11mm2, adj f25,f75,f124,f125
  f124: cylinder r=0.8mm len=15.36mm, axis (0,-1,0), area 15.1mm2, adj f25,f76,f123,f126
  f125: cylinder r=0.8mm len=15.38mm, axis (0,1,0), area 15.5mm2, adj f25,f74,f75,f102,f123,f126
  f126: cylinder r=0.8mm len=11.35mm, axis (-1,0,0), area 11mm2, adj f25,f74,f124,f125
  f127: torus R=4.8mm, axis (0,0,1), area 33.9mm2, adj f24,f25
  f128: cylinder r=0.8mm len=15.36mm, axis (0,1,0), area 15.1mm2, adj f21,f79,f129,f130
  f129: cylinder r=0.8mm len=11.36mm, axis (-1,0,0), area 11mm2, adj f21,f77,f128,f131
  f130: cylinder r=0.8mm len=11.36mm, axis (1,0,0), area 11mm2, adj f21,f80,f128,f131
  f131: cylinder r=0.8mm len=15.36mm, axis (0,-1,0), area 15.1mm2, adj f21,f78,f129,f130
  f132: torus R=4.8mm, axis (0,0,1), area 33.9mm2, adj f20,f21
  f133: torus R=4.8mm, axis (0,0,1), area 33.9mm2, adj f30,f31
  f134: cylinder r=0.8mm len=15.36mm, axis (0,1,0), area 15.1mm2, adj f31,f94,f135,f136
  f135: cylinder r=0.8mm len=11.36mm, axis (-1,0,0), area 11mm2, adj f31,f96,f134,f137
  f136: cylinder r=0.8mm len=11.36mm, axis (-1,0,0), area 11mm2, adj f31,f95,f134,f137
  f137: cylinder r=0.8mm len=15.36mm, axis (0,-1,0), area 15.1mm2, adj f31,f97,f135,f136
  f138: cylinder r=0.8mm len=15.36mm, axis (0,1,0), area 15.1mm2, adj f35,f88,f139,f140
  f139: cylinder r=0.8mm len=11.36mm, axis (-1,0,0), area 11mm2, adj f35,f87,f138,f141
  f140: cylinder r=0.8mm len=11.36mm, axis (-1,0,0), area 11mm2, adj f35,f89,f138,f141
  f141: cylinder r=0.8mm len=15.36mm, axis (0,-1,0), area 15.1mm2, adj f35,f90,f139,f140
  f142: torus R=4.8mm, axis (0,0,1), area 33.9mm2, adj f34,f35
  f143: cylinder r=0.8mm len=26mm, axis (1,0,0), area 31.6mm2, adj f14,f16,f98,f101
PART E: same geometry as B
PLACE A t=(4.74,-5.12,-16.49)mm
PLACE B t=(4.64,-5.12,-19.59)mm
PLACE C t=(4.65,-5.12,-1.49)mm
PLACE D t=(4.29,-5.12,-23.69)mm
PLACE E t=(4.64,-5.12,-26.79)mm
MATE revolute C.f6 <-> A.f9  axis (0,0,-1) through (-44.26,-5.12,-26.49)mm
MATE revolute D.f12 <-> C.f6  axis (0,0,-1) through (-44.26,-5.12,-23.69)mm
MATE revolute C.f6 <-> E.f7  axis (0,0,-1) through (-44.26,-5.12,-26.49)mm
MATE revolute B.f7 <-> C.f6  axis (0,0,-1) through (-44.26,-5.12,-19.59)mm
